# Revit family: ТумбовыйТурникетTTD10AB_Perco
name_source: partatom
category: Оборудование
units: mm (PartAtom-declared; Revit-internal decimal feet)

## family parameters
Всегда вертикально = Да
Классификация = Нет
На основе рабочей плоскости = Нет
Общий = Да
При загрузке вырезать с полостями = Нет
Размер круглого соединителя = Использовать диаметр
Тип детали = Нормальный
Точка расчета площади = Нет

## types (8) — shared parameters
ADSK_URL страницы изделия = https://www.perco.ru
ADSK_Версия семейства = 2019
ADSK_Единица измерения = шт.
ADSK_Завод-изготовитель = PERCo
ADSK_Классификация нагрузок = Турникет
ADSK_Код изделия = PERCo-TTD-10АВ
ADSK_Количество = 1
ADSK_Марка = PERCo
ADSK_Масса = 100
ADSK_Материал = Нержавеющая сталь
ADSK_Наименование = Тумбовый турникет-трипод со встроенной электроникой управления и автоматическими планками Антипаника PERCo-TTD-10АВ
ADSK_Наименование краткое = TTD-10А
ADSK_Напряжение = 12 В
ADSK_Номинальная мощность = 84 Вт
ADSK_Ток = 7 А
L1 = 1058 мм
L2 = 914 мм
t1 = 50 мм
t2 = 36 мм
t3 = 166 мм
Высота = 1024 мм
Высота_лопасть = 895 мм
Габаритные размеры = 1361×750×1024
Глубина = 240 мм
Класс защиты по IEC 61140 = III
Корпус_Срез_Глубина = 29 мм
Ограждение_Отступ = 550 мм
Описание = Нормально открытый электромеханический турникет, предназначен для работы на открытом воздухе (в стандартном варианте исполнения) и внутри помещения
Подключение к электросети = 220В
Пропускная способность = 30 чел/мин
Разработано = https://3dbim.pro
Средняя наработка на отказ, проходов = не менее 4 000 000
Срок службы = 8 лет
Степень защиты  IP = IP55
Стойка_Срез_Катет = 83 мм
Стойка_Ширина = 160 мм
Страна производства = Россия
Температура использования = от -20 до +55 С
Ширина = 1361 мм
Ширина зоны прохода = 560 мм

## per-type parameters (varying)
| type | Тип второй крышки | Тип первой крышки |
| TTD10AB C-10B/C-10Q.1 | КрышкиТурникетаTTD10AB_Perco : PERCo-C-10Q.1 | КрышкиТурникетаTTD10AB_Perco : PERCo-C-10B |
| TTD10AB C-10B/C-10R | КрышкиТурникетаTTD10AB_Perco : PERCo-C-10R | КрышкиТурникетаTTD10AB_Perco : PERCo-C-10B |
| TTD10AB C-10Q.1/C-10Q.1 | КрышкиТурникетаTTD10AB_Perco : PERCo-C-10Q.1 | КрышкиТурникетаTTD10AB_Perco : PERCo-C-10Q.1 |
| TTD10AB C-10Q.1/C-10R | КрышкиТурникетаTTD10AB_Perco : PERCo-C-10R | КрышкиТурникетаTTD10AB_Perco : PERCo-C-10Q.1 |
| TTD10AB C-10R/C-10R | КрышкиТурникетаTTD10AB_Perco : PERCo-C-10R | КрышкиТурникетаTTD10AB_Perco : PERCo-C-10R |
| TTD10AB C-10C/C-10B | КрышкиТурникетаTTD10AB_Perco : PERCo-C-10B | КрышкиТурникетаTTD10AB_Perco : PERCo-C-10С |
| TTD10AB C-10C/C-10Q.1 | КрышкиТурникетаTTD10AB_Perco : PERCo-C-10Q.1 | КрышкиТурникетаTTD10AB_Perco : PERCo-C-10С |
| TTD10AB C-10C/C-10R | КрышкиТурникетаTTD10AB_Perco : PERCo-C-10R | КрышкиТурникетаTTD10AB_Perco : PERCo-C-10С |

## geometry (parser evidence)
native form markers: Blend x4
no freeform markers — native parametric forms only
